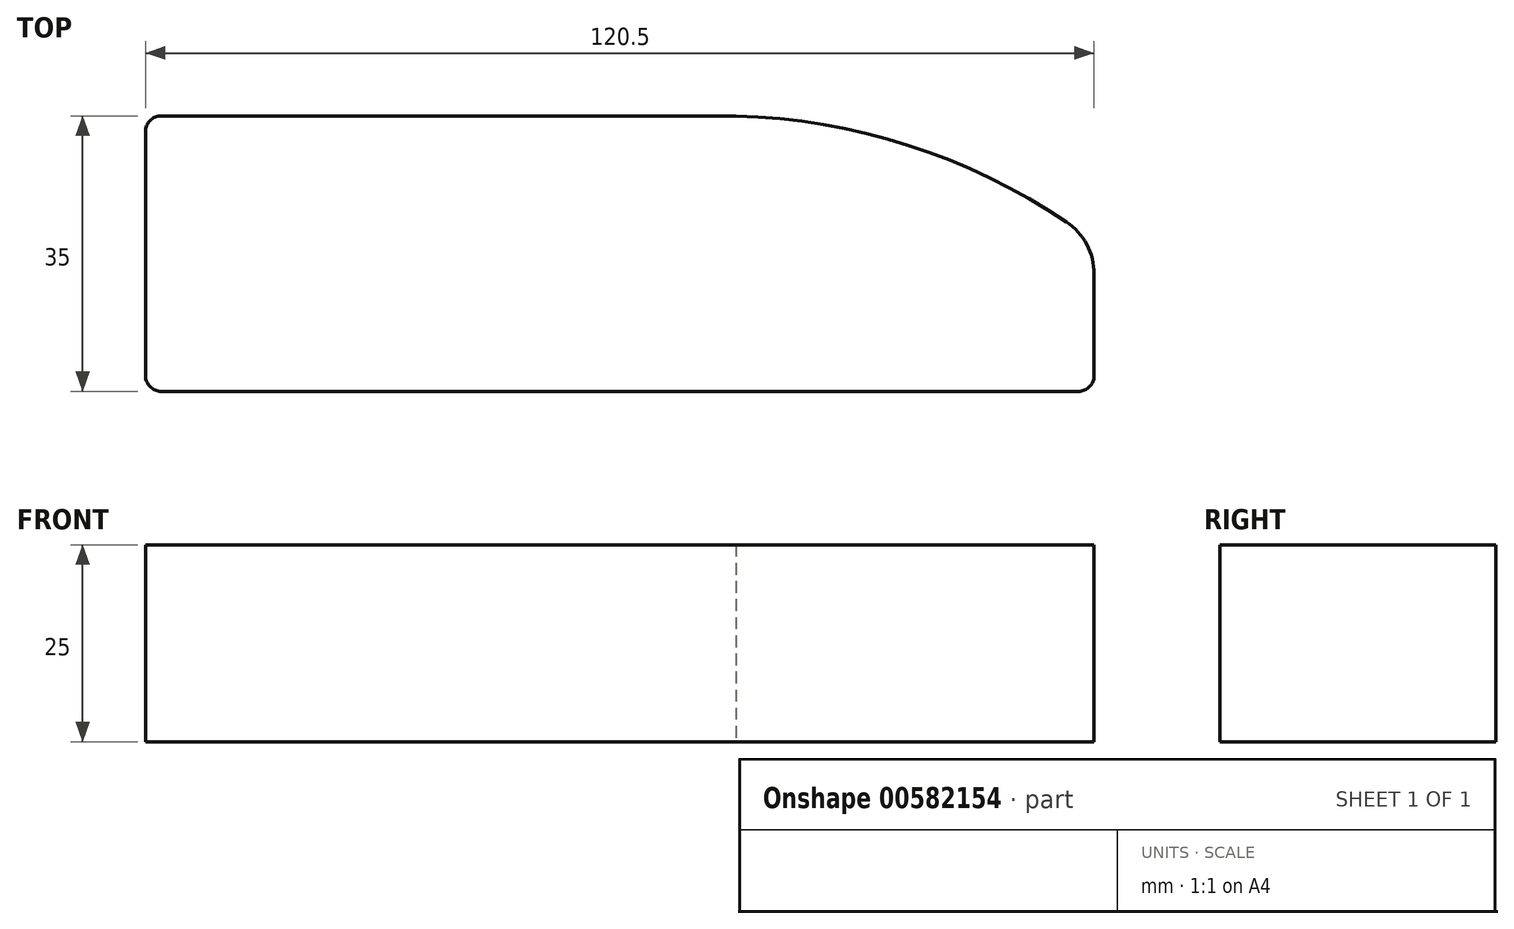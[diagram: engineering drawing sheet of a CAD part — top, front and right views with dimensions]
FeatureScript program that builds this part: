
annotation { "Feature Type Name" : "Feature", "Feature Type Description" : "" }
export const myFeature = defineFeature(function(context is Context, id is Id, definition is map)
    precondition{}
    {
        {
            var Q0;
            Q0=qCreatedBy(makeId("Top.planeOp"),FACE);
            var sketch = newSketch(context, id + "F0", { "sketchPlane" : qUnion([Q0])});
            skLineSegment(sketch, "E0", {"start": v(66.1, -23.75) * mm, "end": v(-54.4, -23.75) * mm});
            skLineSegment(sketch, "E1", {"start": v(-54.4, -23.75) * mm, "end": v(-54.4, 11.25) * mm});
            skLineSegment(sketch, "E2", {"start": v(-54.4, 11.25) * mm, "end": v(20.6, 11.25) * mm});
            skLineSegment(sketch, "E3", {"start": v(66.1, -23.75) * mm, "end": v(66.1, -4.75) * mm});
            skArc(sketch, "E4", {"start": v(66.1, -4.75) * mm, "mid": v(44.59, 6.8) * mm, "end": v(20.6, 11.25) * mm});
            skLineSegment(sketch, "E5", {"start": v(46.1, -23.75) * mm, "end": v(46.1, 6.25) * mm, "construction": true});
            skSolve(sketch);
        }
        {
            var Q0;
            Q0=makeQuery(id+"F0.imprint","IMPRINT",FACE,{"disambiguationData":[TD([[makeQuery(id+"F0.imprint","IMPRINT",EDGE,{"derivedFrom":sQuery(id+"F0.wireOp",EDGE,"E0")}),-1.0]])]});
            extrude(context, id + "F1", {"entities" : qUnion([Q0]), "depth" : 25 * mm, "offsetDistance" : 25 * mm});
        }
        {
            var Q0;
            Q0=makeQuery(id+"F1.opExtrude","SWEPT_EDGE",EDGE,{"disambiguationData":[OSD([sQuery(id+"F0.wireOp",EDGE,"E0"),sQuery(id+"F0.wireOp",EDGE,"E1")])]});
            var Q1;
            Q1=makeQuery(id+"F1.opExtrude","SWEPT_EDGE",EDGE,{"disambiguationData":[OSD([sQuery(id+"F0.wireOp",EDGE,"E0"),sQuery(id+"F0.wireOp",EDGE,"E3")])]});
            var Q2;
            Q2=makeQuery(id+"F1.opExtrude","SWEPT_EDGE",EDGE,{"disambiguationData":[OSD([sQuery(id+"F0.wireOp",EDGE,"E1"),sQuery(id+"F0.wireOp",EDGE,"E2")])]});
            fillet(context, id + "F2", {"entities" : qUnion([Q0, Q1, Q2]), "radius" : 2 * mm, "tangentPropagation" : true, "allowEdgeOverflow" : false});
        }
        {
            var Q0;
            Q0=makeQuery(id+"F1.opExtrude","SWEPT_EDGE",EDGE,{"disambiguationData":[OSD([sQuery(id+"F0.wireOp",EDGE,"E3"),sQuery(id+"F0.wireOp",EDGE,"E4")])]});
            fillet(context, id + "F3", {"entities" : qUnion([Q0]), "radius" : 8 * mm, "tangentPropagation" : true, "allowEdgeOverflow" : false});
        }
    });
